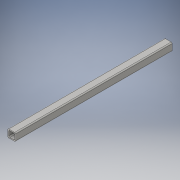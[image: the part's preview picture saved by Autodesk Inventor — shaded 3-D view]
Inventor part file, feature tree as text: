
AUTODESK INVENTOR PART (.ipt)
format: ipt  version: 2016 (Build 200138000, 138)  size: 113,152 bytes
history: native  units: in
note: dims shown in document units (in); Inventor stores cm internally (conversion verified against a paired STEP export)
features: extrude x1, sketch x1
ambient origin geometry x8: Origin, YZ Plane, XZ Plane, XY Plane, X Axis, Y Axis, Z Axis, Center Point
bodies: Solid1 (feature_tree)
feature tree (2):
  extrude  "Extrusion1"  Depth=1.0in
  sketch  "Sketch1"  dims[d0=1.0in d1=1.0in d2=0.125in d3=0.125in d4=20.0in d5=0.0in]
